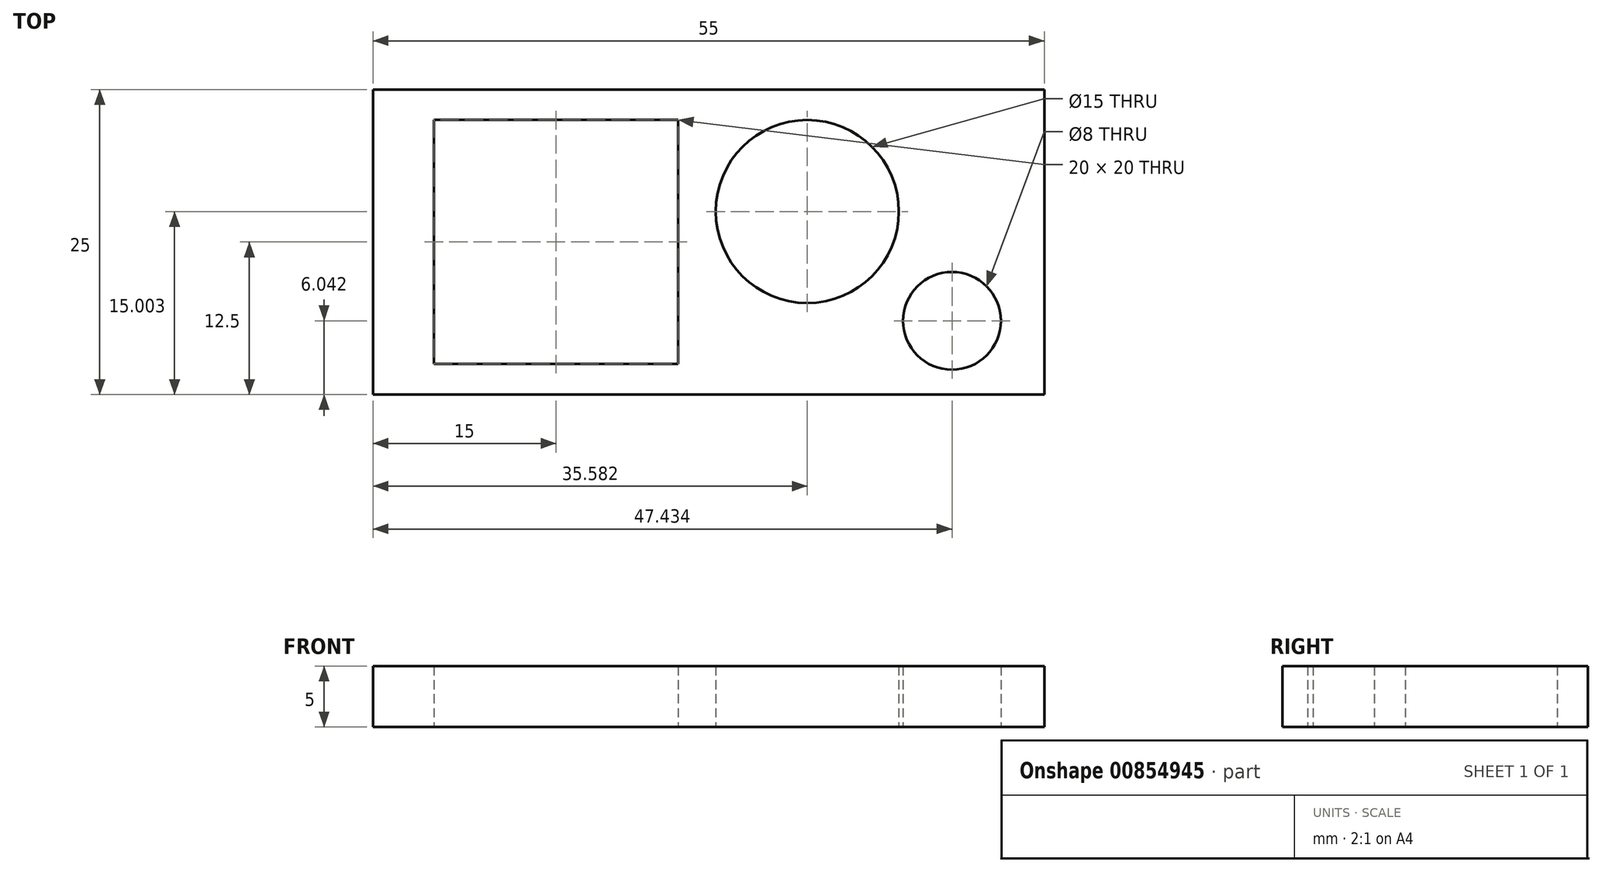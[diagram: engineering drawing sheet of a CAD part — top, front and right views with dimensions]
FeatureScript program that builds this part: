
annotation { "Feature Type Name" : "Feature", "Feature Type Description" : "" }
export const myFeature = defineFeature(function(context is Context, id is Id, definition is map)
    precondition{}
    {
        {
            var Q0;
            Q0=qCreatedBy(makeId("Top.planeOp"),FACE);
            var sketch = newSketch(context, id + "F0", { "sketchPlane" : qUnion([Q0])});
            skLineSegment(sketch, "E0.bottom", {"start": v(10, -10) * mm, "end": v(-10, -10) * mm});
            skLineSegment(sketch, "E0.top", {"start": v(10, 10) * mm, "end": v(-10, 10) * mm});
            skLineSegment(sketch, "E0.left", {"start": v(10, -10) * mm, "end": v(10, 10) * mm});
            skLineSegment(sketch, "E0.right", {"start": v(-10, -10) * mm, "end": v(-10, 10) * mm});
            skPoint(sketch, "E0.middle", {"position": v(0, 0) * mm});
            skCircle(sketch, "E1", {"center": v(20.58, 2.5) * mm, "radius": 7.5 * mm});
            skCircle(sketch, "E2", {"center": v(32.43, -6.46) * mm, "radius": 4 * mm});
            skLineSegment(sketch, "E3.bottom", {"start": v(-15, 12.5) * mm, "end": v(40, 12.5) * mm});
            skLineSegment(sketch, "E3.top", {"start": v(-15, -12.5) * mm, "end": v(40, -12.5) * mm});
            skLineSegment(sketch, "E3.left", {"start": v(-15, 12.5) * mm, "end": v(-15, -12.5) * mm});
            skLineSegment(sketch, "E3.right", {"start": v(40, 12.5) * mm, "end": v(40, -12.5) * mm});
            skSolve(sketch);
        }
        {
            var Q0;
            Q0=makeQuery(id+"F0.imprint","IMPRINT",FACE,{"disambiguationData":[TD([[makeQuery(id+"F0.imprint","IMPRINT",EDGE,{"derivedFrom":sQuery(id+"F0.wireOp",EDGE,"E0.bottom")}),1.0]])]});
            extrude(context, id + "F1", {"entities" : qUnion([Q0]), "depth" : 5 * mm, "offsetDistance" : 25 * mm});
        }
    });
